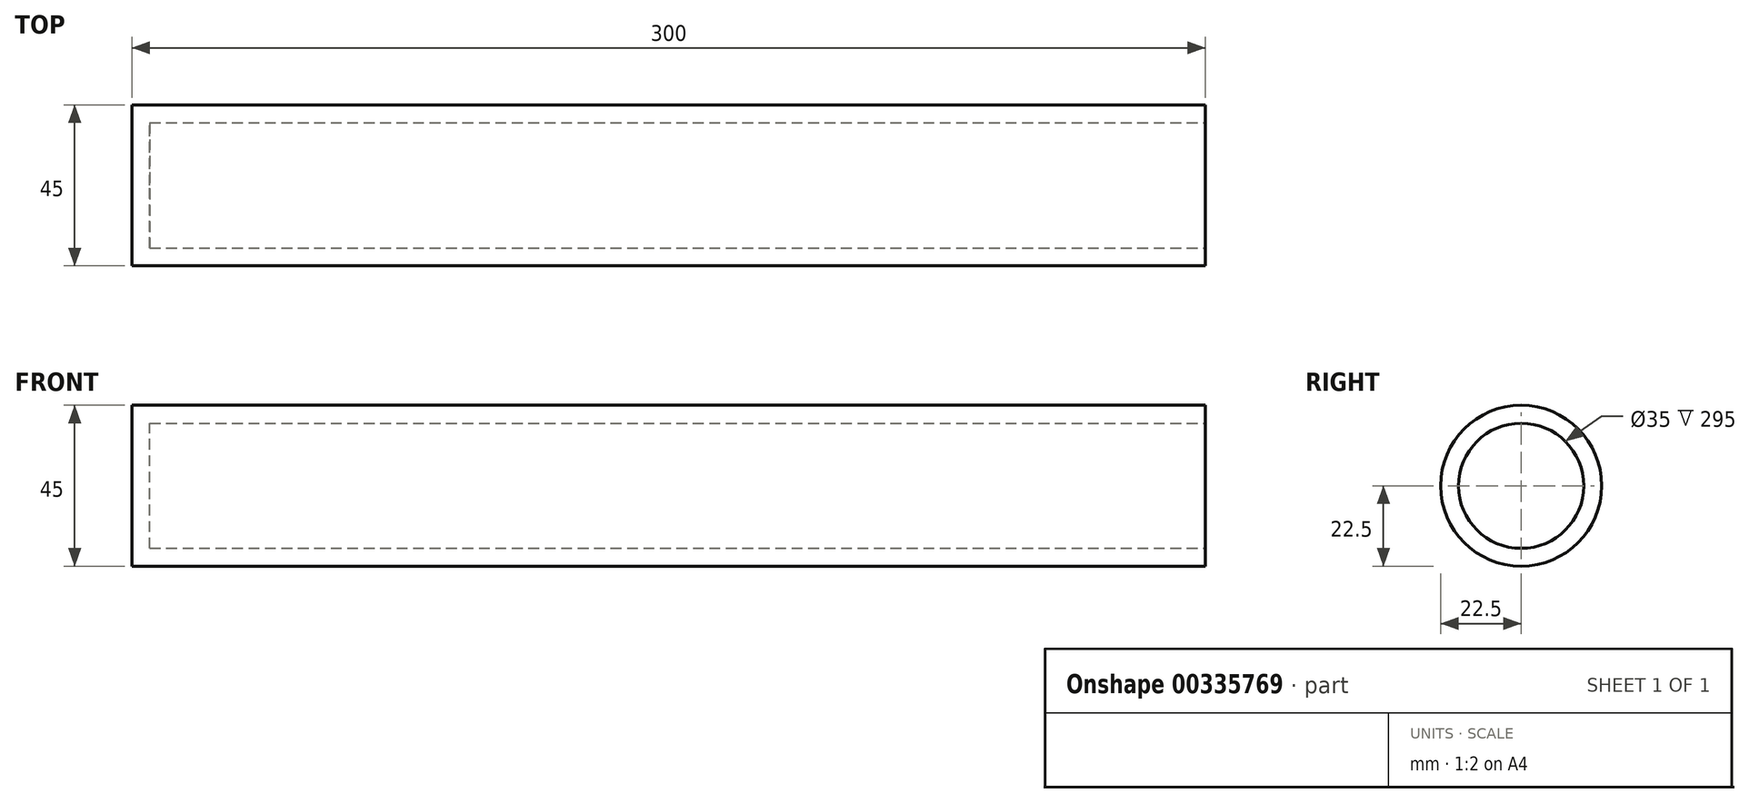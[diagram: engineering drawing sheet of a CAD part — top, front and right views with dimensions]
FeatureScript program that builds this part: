
annotation { "Feature Type Name" : "Feature", "Feature Type Description" : "" }
export const myFeature = defineFeature(function(context is Context, id is Id, definition is map)
    precondition{}
    {
        {
            var Q0;
            Q0=qCreatedBy(makeId("Right.planeOp"),FACE);
            var sketch = newSketch(context, id + "F0", { "sketchPlane" : qUnion([Q0])});
            skCircle(sketch, "E0", {"center": v(0, 0) * mm, "radius": 22.5 * mm});
            skSolve(sketch);
        }
        {
            var Q0;
            Q0=makeQuery(id+"F0.imprint","IMPRINT",FACE,{"disambiguationData":[TD([[makeQuery(id+"F0.imprint","IMPRINT",EDGE,{"derivedFrom":sQuery(id+"F0.wireOp",EDGE,"E0")}),1.0]])]});
            extrude(context, id + "F1", {"entities" : qUnion([Q0]), "oppositeDirection" : true, "depth" : 300 * mm});
        }
        {
            var Q0;
            Q0=makeQuery(id+"F1.opExtrude","CAP_FACE",FACE,{"disambiguationData":[OSD([sQuery(id+"F0.wireOp",EDGE,"E0")])],"isStart":true});
            shell(context, id + "F2", {"entities" : qUnion([Q0]), "thickness" : 5 * mm});
        }
    });
